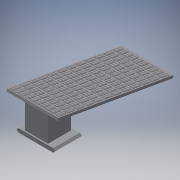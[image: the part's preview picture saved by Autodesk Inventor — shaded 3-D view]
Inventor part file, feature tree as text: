
AUTODESK INVENTOR PART (.ipt)
format: ipt  version: 2018.3 (Build 223284000, 284)  size: 2,990,592 bytes
history: native  units: mm
features: extrude x14, sketch x13, chamfer x6, pattern_linear x4
ambient origin geometry x8: Origin, YZ Plane, XZ Plane, XY Plane, X Axis, Y Axis, Z Axis, Center Point
bodies: Solid1 (feature_tree)
feature tree (37):
  extrude  "Extrusion1"  Depth=1.8mm
  extrude  "Extrusion2"  Depth=1.5mm TaperAngle=0.0deg
  chamfer  "Chamfer2"  Distance=10.0mm
  chamfer  "Chamfer3"  Distance=1.0mm
  extrude  "Extrusion3"  Depth=1.0mm TaperAngle=0.0deg
  extrude  "Extrusion4"  Depth=18.0mm
  extrude  "Extrusion5"  Depth=9.0mm
  pattern_linear  "Rectangular Pattern1"  Spacing1=9.0mm  [1 undecoded]
  pattern_linear  "Rectangular Pattern2"  Spacing1=6.788202mm  [1 undecoded]
  extrude  "Extrusion6"  Depth=1.4mm
  chamfer  "Chamfer7"  Distance=3.0mm
  chamfer  "Chamfer8"  Distance=0.5mm
  chamfer  "Chamfer9"  Distance=0.5mm
  chamfer  "Chamfer10"  Distance=0.2mm
  extrude  "Extrusion7"  Depth=0.2mm
  extrude  "Extrusion8"  Depth=0.5mm
  extrude  "Extrusion9"  Depth=0.25mm
  extrude  "Extrusion10"  Depth=0.25mm
  extrude  "Extrusion11"  Depth=0.2mm TaperAngle=0.0deg
  extrude  "Extrusion12"  Depth=0.2mm
  extrude  "Extrusion13"  Depth=0.2mm
  extrude  "Extrusion14"  Depth=0.5mm
  pattern_linear  "Rectangular Pattern3"  Spacing1=0.25mm  [1 undecoded]
  pattern_linear  "Rectangular Pattern4"  Spacing1=0.25mm  [1 undecoded]
  sketch  "Sketch2"  dims[d0=1.8mm d2=15.0mm]
  sketch  "Sketch3"  dims[d3=5.5mm d6=1.5mm d7=0.0mm]
  sketch  "Sketch4"  dims[d8=0.5mm]
  sketch  "Sketch5"  dims[d9=3.0mm]
  sketch  "Sketch6"  dims[d10=0.5mm]
  sketch  "Sketch7"  dims[d11=2.0mm]
  sketch  "Sketch8"  dims[d12=0.5mm]
  sketch  "Sketch9"  dims[d13=1.5mm]
  sketch  "Sketch10"  dims[d14=6.25mm]
  sketch  "Sketch11"  dims[d15=6.25mm d16=10.0mm d17=0.0mm d21=0.52mm d22=1.0mm d23=13.962634mm]
  sketch  "Sketch12"  dims[d24=0.52mm d25=1.0mm d26=13.962634mm d27=1.0mm d28=0.0mm]
  sketch  "Sketch13"  dims[d29=18.0mm d30=18.0mm]
  sketch  "Sketch14"  dims[d31=48.5mm d32=9.0mm d33=9.0mm d34=6.788202mm d35=1.4mm d36=3.0mm d37=0.5mm d38=0.5mm d39=0.2mm d40=0.2mm d41=0.5mm d42=0.25mm d43=0.25mm d44=0.2mm d45=0.0mm d46=0.2mm d47=0.2mm d48=0.5mm d49=0.25mm d50=0.25mm d51=0.1mm d52=0.0mm d53=90.0mm d55=1.95mm d56=120.0mm d58=3.7mm d59=10.0mm d60=0.0mm d70=0.75mm d71=2.0mm d72=45.0deg d73=0.75mm d74=2.0mm d75=45.0deg d76=0.75mm d77=2.0mm d78=45.0deg d79=0.75mm d80=2.0mm d81=45.0deg d86=3.0mm d87=0.0mm d88=3.0mm d89=0.0mm d90=5.0mm d91=0.0mm d92=1.0mm d93=0.0mm d94=5.0mm d95=0.0mm d96=9.0mm d97=0.0mm d98=2.0mm d99=0.0mm d100=3.0mm d101=0.0mm d102=20.0mm d104=1.95mm d105=120.0mm d107=3.7mm]
note: 4 required parameter values undecoded (feature->parameter linkage not recoverable at this tier; creation-order binding heuristic only, values carry confidence <= 0.55)
